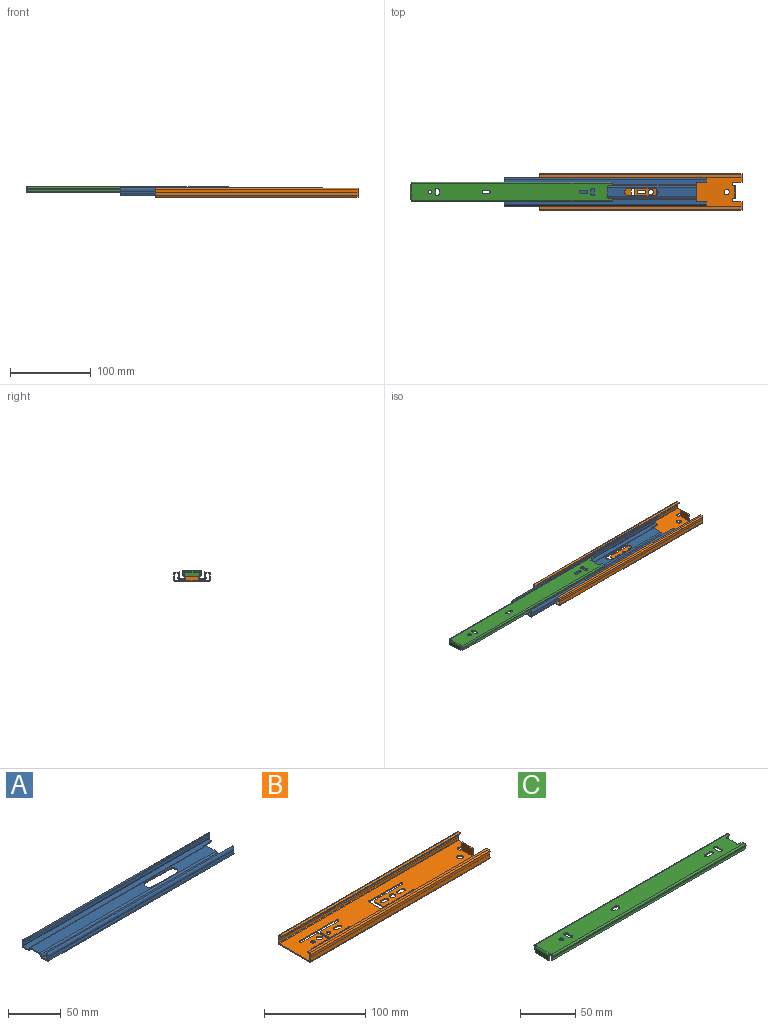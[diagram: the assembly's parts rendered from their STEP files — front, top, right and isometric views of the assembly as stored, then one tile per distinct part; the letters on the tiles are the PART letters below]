
ASSEMBLY  parts=3 mates=2
PART A: 42 faces, bbox 249.9x35.2x9.3 mm
  f0: cylinder r=4.83mm len=9.65mm, axis (0,0,1), area 18.5mm2, adj f1,f16,f23,f41
  f1: plane 237.24x12.23mm, normal (0,0,-1), area 2522.2mm2, adj f0,f2,f18,f20,f22,f23,f24,f41
  f2: cylinder r=0.76mm len=237.24mm, axis (-1,0,0), area 205.1mm2, adj f1,f3,f18,f20
  f3: plane 237.24x1.97mm, normal (0,-0.91,-0.42), area 516.2mm2, adj f2,f4,f18,f20
  f4: cylinder r=1.98mm len=237.24mm, axis (-1,0,0), area 533.2mm2, adj f3,f5,f18,f20
  f5: plane 249.94x6.86mm, normal (0,0,-1), area 1682.4mm2, adj f4,f6,f17,f18,f19,f20,f21
  f6: cylinder r=1.22mm len=249.94mm, axis (-1,0,0), area 698.7mm2, adj f5,f7,f17,f18
  f7: cylinder r=2.51mm len=249.94mm, axis (-1,0,0), area 734.3mm2, adj f6,f8,f17,f18
  f8: cylinder r=3.52mm len=249.94mm, axis (-1,0,0), area 1279.5mm2, adj f7,f9,f17,f18
  f9: plane 249.94x1.03mm, normal (0,-0.84,0.54), area 304.7mm2, adj f8,f10,f17,f18
  f10: cylinder r=2.3mm len=249.94mm, axis (-1,0,0), area 836mm2, adj f9,f11,f17,f18
  f11: cylinder r=3.73mm len=249.94mm, axis (-1,0,0), area 1091.1mm2, adj f10,f12,f17,f18
  f12: plane 249.94x6.86mm, normal (0,0,1), area 1682.4mm2, adj f11,f13,f17,f18,f19,f20,f21
  f13: cylinder r=0.76mm len=237.24mm, axis (-1,0,0), area 205.1mm2, adj f12,f14,f18,f20
  f14: plane 237.24x1.97mm, normal (0,0.91,0.42), area 516.2mm2, adj f13,f15,f18,f20
  f15: cylinder r=1.98mm len=237.24mm, axis (-1,0,0), area 533.2mm2, adj f14,f16,f18,f20
  f16: plane 237.24x12.23mm, normal (0,0,1), area 2522.2mm2, adj f0,f15,f18,f20,f22,f23,f37,f41
  f17: plane 9.27x5.53mm, normal (1,0,0), area 16.6mm2, adj f5,f6,f7,f8,f9,f10,f11,f12
  f18: plane 35.19x9.27mm, normal (-1,0,0), area 67.2mm2, adj f1,f2,f3,f4,f5,f6,f7,f8
  f19: cylinder r=2.54mm len=2.54mm, axis (0,0,1), area 4.9mm2, adj f5,f12,f20,f21
  f20: plane 19.05x4.78mm, normal (1,0,0), area 27.8mm2, adj f1,f2,f3,f4,f5,f12,f13,f14
  f21: plane 10.16x1.22mm, normal (0,-1,0), area 12.4mm2, adj f5,f12,f17,f19
  f22: cylinder r=4.83mm len=9.65mm, axis (0,0,1), area 18.5mm2, adj f1,f16,f23,f41
  f23: plane 31.75x1.22mm, normal (0,-1,0), area 38.7mm2, adj f0,f1,f16,f22
  f24: cylinder r=0.76mm len=237.24mm, axis (-1,0,0), area 205.1mm2, adj f1,f18,f20,f25
  f25: plane 237.24x1.97mm, normal (0,0.91,-0.42), area 516.2mm2, adj f18,f20,f24,f26
  f26: cylinder r=1.98mm len=237.24mm, axis (-1,0,0), area 533.2mm2, adj f18,f20,f25,f27
  f27: plane 249.94x6.86mm, normal (0,0,-1), area 1682.4mm2, adj f18,f20,f26,f28,f38,f39,f40
  f28: cylinder r=1.22mm len=249.94mm, axis (-1,0,0), area 698.7mm2, adj f18,f27,f29,f38
  f29: cylinder r=2.51mm len=249.94mm, axis (-1,0,0), area 734.3mm2, adj f18,f28,f30,f38
  f30: cylinder r=3.52mm len=249.94mm, axis (-1,0,0), area 1279.5mm2, adj f18,f29,f31,f38
  f31: plane 249.94x1.03mm, normal (0,0.84,0.54), area 304.7mm2, adj f18,f30,f32,f38
  f32: cylinder r=2.3mm len=249.94mm, axis (-1,0,0), area 836mm2, adj f18,f31,f33,f38
  f33: cylinder r=3.73mm len=249.94mm, axis (-1,0,0), area 1091.1mm2, adj f18,f32,f34,f38
  f34: plane 249.94x6.86mm, normal (0,0,1), area 1682.4mm2, adj f18,f20,f33,f35,f38,f39,f40
  f35: cylinder r=0.76mm len=237.24mm, axis (-1,0,0), area 205.1mm2, adj f18,f20,f34,f36
  f36: plane 237.24x1.97mm, normal (0,-0.91,0.42), area 516.2mm2, adj f18,f20,f35,f37
  f37: cylinder r=1.98mm len=237.24mm, axis (-1,0,0), area 533.2mm2, adj f16,f18,f20,f36
  f38: plane 9.27x5.53mm, normal (1,0,0), area 16.6mm2, adj f27,f28,f29,f30,f31,f32,f33,f34
  f39: cylinder r=2.54mm len=2.54mm, axis (0,0,1), area 4.9mm2, adj f20,f27,f34,f40
  f40: plane 10.16x1.22mm, normal (0,1,0), area 12.4mm2, adj f27,f34,f38,f39
  f41: plane 31.75x1.22mm, normal (0,1,0), area 38.7mm2, adj f0,f1,f16,f22
PART B: 85 faces, bbox 249.9x45.6x11.3 mm
  f0: cylinder r=1.59mm len=3.18mm, axis (0,0,1), area 6mm2, adj f8,f9,f72,f73
  f1: cylinder r=3.17mm len=6.35mm, axis (0,0,-1), area 23.8mm2, adj f8,f9
  f2: cylinder r=3.17mm len=6.35mm, axis (0,0,-1), area 23.8mm2, adj f8,f9
  f3: cylinder r=2.29mm len=4.57mm, axis (0,0,1), area 8.6mm2, adj f8,f9,f40,f77
  f4: cylinder r=2.29mm len=4.57mm, axis (0,0,1), area 17.1mm2, adj f8,f9
  f5: cylinder r=3.17mm len=6.35mm, axis (0,0,1), area 23.8mm2, adj f8,f9
  f6: cylinder r=2.29mm len=4.57mm, axis (0,0,1), area 17.1mm2, adj f8,f9
  f7: cylinder r=1.59mm len=3.18mm, axis (0,0,1), area 6mm2, adj f8,f9,f32,f33
  f8: plane 249.94x42.24mm, normal (0,0,1), area 9331.9mm2, adj f0,f1,f2,f3,f4,f5,f6,f7
  f9: plane 249.94x42.24mm, normal (0,0,-1), area 9352.8mm2, adj f0,f1,f2,f3,f4,f5,f6,f7
  f10: cylinder r=1.7mm len=249.94mm, axis (-1,0,0), area 679.3mm2, adj f9,f11,f22,f23
  f11: plane 249.94x4.64mm, normal (0,1,0.03), area 1159mm2, adj f10,f12,f22,f23
  f12: plane 249.94x3.4mm, normal (0,1,-0.04), area 849.3mm2, adj f11,f13,f22,f23
  f13: cylinder r=1.45mm len=249.94mm, axis (-1,0,0), area 581.3mm2, adj f12,f14,f22,f23
  f14: plane 249.94x2.96mm, normal (0,0,1), area 739.4mm2, adj f13,f15,f22,f23
  f15: plane 249.94x1.19mm, normal (0,-1,0), area 298.4mm2, adj f14,f16,f22,f23
  f16: plane 249.94x2.96mm, normal (0,0,-1), area 739.4mm2, adj f15,f17,f22,f23
  f17: cylinder r=0.25mm len=249.94mm, axis (-1,0,0), area 102mm2, adj f16,f18,f22,f23
  f18: plane 249.94x3.05mm, normal (0,-1,0.04), area 763mm2, adj f17,f19,f22,f23
  f19: cylinder r=2.54mm len=249.94mm, axis (-1,0,0), area 484.9mm2, adj f18,f20,f22,f23
  f20: plane 249.94x3.16mm, normal (0,-1,-0.03), area 790.5mm2, adj f19,f21,f22,f23
  f21: cylinder r=0.51mm len=249.94mm, axis (-1,0,0), area 202.8mm2, adj f8,f20,f22,f23
  f22: plane 11.28x10.62mm, normal (1,0,0), area 27.3mm2, adj f8,f9,f10,f11,f12,f13,f14,f15
  f23: plane 45.64x11.28mm, normal (-1,0,0), area 83.7mm2, adj f8,f9,f10,f11,f12,f13,f14,f15
  f24: plane 14.99x10.08mm, normal (1,0,0), area 151.1mm2, adj f9,f25,f28,f30,f67,f70
  f25: plane 1.43x1.19mm, normal (0.11,0.99,0), area 1.7mm2, adj f8,f9,f24,f26
  f26: cylinder r=2.29mm len=4.56mm, axis (0,0,1), area 8.3mm2, adj f8,f9,f25,f27
  f27: plane 9.4x1.19mm, normal (0,-1,0), area 11.2mm2, adj f8,f9,f22,f26
  f28: plane 8.89x1.4mm, normal (0,1,0), area 12.4mm2, adj f8,f24,f29,f30
  f29: plane 14.99x8.89mm, normal (-1,0,0), area 133.2mm2, adj f8,f28,f30,f70
  f30: plane 14.99x1.4mm, normal (0,0,1), area 20.9mm2, adj f24,f28,f29,f70
  f31: cylinder r=1.59mm len=3.18mm, axis (0,0,1), area 6mm2, adj f8,f9,f32,f38
  f32: plane 50.93x1.19mm, normal (0,-1,0), area 60.8mm2, adj f7,f8,f9,f31
  f33: plane 24.83x1.19mm, normal (0,1,0), area 29.6mm2, adj f7,f8,f9,f34
  f34: cylinder r=0.76mm len=1.19mm, axis (0,0,1), area 1.4mm2, adj f8,f9,f33,f35
  f35: plane 12.7x1.19mm, normal (-1,0,0), area 15.2mm2, adj f8,f9,f34,f74
  f36: plane 12.7x1.19mm, normal (1,0,0), area 15.2mm2, adj f8,f9,f37,f75
  f37: cylinder r=0.76mm len=1.19mm, axis (0,0,1), area 1.4mm2, adj f8,f9,f36,f38
  f38: plane 22.29x1.19mm, normal (0,1,0), area 26.6mm2, adj f8,f9,f31,f37
  f39: cylinder r=2.29mm len=4.57mm, axis (0,0,1), area 8.6mm2, adj f8,f9,f40,f77
  f40: plane 5.08x1.19mm, normal (0,-1,0), area 6.1mm2, adj f3,f8,f9,f39
  f41: cylinder r=1.59mm len=3.18mm, axis (0,0,-1), area 6mm2, adj f8,f9,f42,f47
  f42: plane 43.24x1.19mm, normal (0,-1,0), area 51.6mm2, adj f8,f9,f41,f43
  f43: cylinder r=1.52mm len=1.52mm, axis (0,0,-1), area 2.9mm2, adj f8,f9,f42,f44
  f44: plane 17.53x1.19mm, normal (1,0,0), area 20.9mm2, adj f8,f9,f43,f80
  f45: plane 11.18x1.19mm, normal (-1,0,0), area 13.3mm2, adj f8,f9,f46,f81
  f46: cylinder r=1.52mm len=1.52mm, axis (0,0,-1), area 2.9mm2, adj f8,f9,f45,f47
  f47: plane 38.67x1.19mm, normal (0,1,0), area 46.2mm2, adj f8,f9,f41,f46
  f48: cylinder r=2.29mm len=4.57mm, axis (0,0,-1), area 8.6mm2, adj f8,f9,f49,f83
  f49: plane 5.08x1.19mm, normal (0,-1,0), area 6.1mm2, adj f8,f9,f48,f50
  f50: cylinder r=2.29mm len=4.57mm, axis (0,0,-1), area 8.6mm2, adj f8,f9,f49,f83
  f51: cylinder r=2.29mm len=4.57mm, axis (0,0,-1), area 8.6mm2, adj f8,f9,f52,f84
  f52: plane 5.08x1.19mm, normal (0,-1,0), area 6.1mm2, adj f8,f9,f51,f53
  f53: cylinder r=2.29mm len=4.57mm, axis (0,0,-1), area 8.6mm2, adj f8,f9,f52,f84
  f54: cylinder r=1.7mm len=249.94mm, axis (-1,0,0), area 679.3mm2, adj f9,f23,f55,f66
  f55: plane 249.94x4.64mm, normal (0,-1,0.03), area 1159mm2, adj f23,f54,f56,f66
  f56: plane 249.94x3.4mm, normal (0,-1,-0.04), area 849.3mm2, adj f23,f55,f57,f66
  f57: cylinder r=1.45mm len=249.94mm, axis (-1,0,0), area 581.3mm2, adj f23,f56,f58,f66
  f58: plane 249.94x2.96mm, normal (0,0,1), area 739.4mm2, adj f23,f57,f59,f66
  f59: plane 249.94x1.19mm, normal (0,1,0), area 298.4mm2, adj f23,f58,f60,f66
  f60: plane 249.94x2.96mm, normal (0,0,-1), area 739.4mm2, adj f23,f59,f61,f66
  f61: cylinder r=0.25mm len=249.94mm, axis (-1,0,0), area 102mm2, adj f23,f60,f62,f66
  f62: plane 249.94x3.05mm, normal (0,1,0.04), area 763mm2, adj f23,f61,f63,f66
  f63: cylinder r=2.54mm len=249.94mm, axis (-1,0,0), area 484.9mm2, adj f23,f62,f64,f66
  f64: plane 249.94x3.16mm, normal (0,1,-0.03), area 790.5mm2, adj f23,f63,f65,f66
  f65: cylinder r=0.51mm len=249.94mm, axis (-1,0,0), area 202.8mm2, adj f8,f23,f64,f66
  f66: plane 11.28x10.62mm, normal (1,0,0), area 27.3mm2, adj f8,f9,f54,f55,f56,f57,f58,f59
  f67: plane 1.43x1.19mm, normal (0.11,-0.99,0), area 1.7mm2, adj f8,f9,f24,f68
  f68: cylinder r=2.29mm len=4.56mm, axis (0,0,1), area 8.3mm2, adj f8,f9,f67,f69
  f69: plane 9.4x1.19mm, normal (0,1,0), area 11.2mm2, adj f8,f9,f66,f68
  f70: plane 8.89x1.4mm, normal (0,-1,0), area 12.4mm2, adj f8,f24,f29,f30
  f71: cylinder r=1.59mm len=3.18mm, axis (0,0,1), area 6mm2, adj f8,f9,f72,f76
  f72: plane 50.93x1.19mm, normal (0,1,0), area 60.8mm2, adj f0,f8,f9,f71
  f73: plane 24.83x1.19mm, normal (0,-1,0), area 29.6mm2, adj f0,f8,f9,f74
  f74: cylinder r=0.76mm len=1.19mm, axis (0,0,1), area 1.4mm2, adj f8,f9,f35,f73
  f75: cylinder r=0.76mm len=1.19mm, axis (0,0,1), area 1.4mm2, adj f8,f9,f36,f76
  f76: plane 22.29x1.19mm, normal (0,-1,0), area 26.6mm2, adj f8,f9,f71,f75
  f77: plane 5.08x1.19mm, normal (0,1,0), area 6.1mm2, adj f3,f8,f9,f39
  f78: cylinder r=1.59mm len=3.18mm, axis (0,0,-1), area 6mm2, adj f8,f9,f79,f82
  f79: plane 43.24x1.19mm, normal (0,1,0), area 51.6mm2, adj f8,f9,f78,f80
  f80: cylinder r=1.52mm len=1.52mm, axis (0,0,-1), area 2.9mm2, adj f8,f9,f44,f79
  f81: cylinder r=1.52mm len=1.52mm, axis (0,0,-1), area 2.9mm2, adj f8,f9,f45,f82
  f82: plane 38.67x1.19mm, normal (0,-1,0), area 46.2mm2, adj f8,f9,f78,f81
  f83: plane 5.08x1.19mm, normal (0,1,0), area 6.1mm2, adj f8,f9,f48,f50
  f84: plane 5.08x1.19mm, normal (0,1,0), area 6.1mm2, adj f8,f9,f51,f53
PART C: 54 faces, bbox 249.9x24.3x6.8 mm
  f0: cylinder r=2.16mm len=4.32mm, axis (0,0,1), area 9.5mm2, adj f3,f13,f34,f53
  f1: cylinder r=2.16mm len=4.32mm, axis (0,0,1), area 9.5mm2, adj f3,f13,f29,f51
  f2: cylinder r=2.29mm len=4.57mm, axis (0,0,1), area 20.1mm2, adj f3,f13
  f3: plane 248.29x21.25mm, normal (0,0,-1), area 5015.5mm2, adj f0,f1,f2,f4,f14,f15,f16,f21
  f4: cylinder r=0.13mm len=248.03mm, axis (-1,0,0), area 49.5mm2, adj f3,f5,f14,f15
  f5: plane 248.03x0.37mm, normal (0,-1,0), area 92.5mm2, adj f4,f6,f14,f15
  f6: cylinder r=0.13mm len=248.03mm, axis (-1,0,0), area 20.6mm2, adj f5,f7,f14,f15
  f7: cylinder r=3.81mm len=248.03mm, axis (-1,0,0), area 1283.1mm2, adj f6,f8,f14,f15
  f8: plane 248.03x1.07mm, normal (0,0.65,-0.76), area 346.5mm2, adj f7,f9,f14,f15
  f9: cylinder r=2.41mm len=248.03mm, axis (-1,0,0), area 812.4mm2, adj f8,f10,f14,f15
  f10: cylinder r=1.52mm len=248.03mm, axis (-1,0,0), area 247.4mm2, adj f9,f11,f14,f15
  f11: plane 248.03x0.37mm, normal (0,1,0), area 92.5mm2, adj f10,f12,f14,f15
  f12: cylinder r=1.52mm len=248.03mm, axis (-1,0,0), area 593.8mm2, adj f11,f13,f14,f15
  f13: plane 248.29x21.25mm, normal (0,0,1), area 5015.5mm2, adj f0,f1,f2,f12,f14,f15,f20,f21
  f14: plane 6.76x3.56mm, normal (1,0,0), area 11.8mm2, adj f3,f4,f5,f6,f7,f8,f9,f10
  f15: plane 6.76x3.26mm, normal (-1,0,0), area 11.4mm2, adj f3,f4,f5,f6,f7,f8,f9,f10
  f16: cylinder r=0.25mm len=17.78mm, axis (0,-1,0), area 7.1mm2, adj f3,f17,f21,f46
  f17: plane 17.78x5.11mm, normal (1,0,0), area 90.8mm2, adj f16,f18,f21,f46
  f18: plane 17.78x1.4mm, normal (0,0,-1), area 24.8mm2, adj f17,f19,f21,f46
  f19: plane 17.78x5.11mm, normal (-1,0,0), area 90.8mm2, adj f18,f20,f21,f46
  f20: cylinder r=1.65mm len=17.78mm, axis (0,-1,0), area 46.1mm2, adj f13,f19,f21,f46
  f21: plane 6.76x1.91mm, normal (0,1,0), area 9.6mm2, adj f3,f13,f15,f16,f17,f18,f19,f20
  f22: cylinder r=0.63mm len=1.4mm, axis (0,0,1), area 2.6mm2, adj f3,f13,f23,f24
  f23: plane 5.86x1.4mm, normal (0.23,-0.97,0), area 8.4mm2, adj f3,f13,f14,f22
  f24: plane 5.97x1.4mm, normal (1,0,0), area 8.3mm2, adj f3,f13,f22,f49
  f25: cylinder r=2.16mm len=4.32mm, axis (0,0,1), area 9.5mm2, adj f3,f13,f26,f27
  f26: plane 5.33x1.4mm, normal (-1,0,0), area 7.5mm2, adj f3,f13,f25,f50
  f27: plane 5.33x1.4mm, normal (1,0,0), area 7.5mm2, adj f3,f13,f25,f50
  f28: cylinder r=2.16mm len=4.32mm, axis (0,0,1), area 9.5mm2, adj f3,f13,f29,f51
  f29: plane 5.33x1.4mm, normal (0,-1,0), area 7.5mm2, adj f1,f3,f13,f28
  f30: plane 5.33x1.4mm, normal (1,0,0), area 7.5mm2, adj f3,f13,f31,f52
  f31: cylinder r=2.16mm len=4.32mm, axis (0,0,1), area 9.5mm2, adj f3,f13,f30,f32
  f32: plane 5.33x1.4mm, normal (-1,0,0), area 7.5mm2, adj f3,f13,f31,f52
  f33: cylinder r=2.16mm len=4.32mm, axis (0,0,1), area 9.5mm2, adj f3,f13,f34,f53
  f34: plane 5.33x1.4mm, normal (0,-1,0), area 7.5mm2, adj f0,f3,f13,f33
  f35: cylinder r=0.13mm len=248.03mm, axis (-1,0,0), area 49.5mm2, adj f3,f36,f44,f45
  f36: plane 248.03x0.37mm, normal (0,1,0), area 92.5mm2, adj f35,f37,f44,f45
  f37: cylinder r=0.13mm len=248.03mm, axis (-1,0,0), area 20.6mm2, adj f36,f38,f44,f45
  f38: cylinder r=3.81mm len=248.03mm, axis (-1,0,0), area 1283.1mm2, adj f37,f39,f44,f45
  f39: plane 248.03x1.07mm, normal (0,-0.65,-0.76), area 346.5mm2, adj f38,f40,f44,f45
  f40: cylinder r=2.41mm len=248.03mm, axis (-1,0,0), area 812.4mm2, adj f39,f41,f44,f45
  f41: cylinder r=1.52mm len=248.03mm, axis (-1,0,0), area 247.4mm2, adj f40,f42,f44,f45
  f42: plane 248.03x0.37mm, normal (0,-1,0), area 92.5mm2, adj f41,f43,f44,f45
  f43: cylinder r=1.52mm len=248.03mm, axis (-1,0,0), area 593.8mm2, adj f13,f42,f44,f45
  f44: plane 6.76x3.56mm, normal (1,0,0), area 11.8mm2, adj f3,f13,f35,f36,f37,f38,f39,f40
  f45: plane 6.76x3.26mm, normal (-1,0,0), area 11.4mm2, adj f3,f13,f35,f36,f37,f38,f39,f40
  f46: plane 6.76x1.91mm, normal (0,-1,0), area 9.6mm2, adj f3,f13,f16,f17,f18,f19,f20,f45
  f47: cylinder r=0.63mm len=1.4mm, axis (0,0,1), area 2.6mm2, adj f3,f13,f48,f49
  f48: plane 5.86x1.4mm, normal (0.23,0.97,0), area 8.4mm2, adj f3,f13,f44,f47
  f49: plane 5.97x1.4mm, normal (1,0,0), area 8.3mm2, adj f3,f13,f24,f47
  f50: cylinder r=2.16mm len=4.32mm, axis (0,0,1), area 9.5mm2, adj f3,f13,f26,f27
  f51: plane 5.33x1.4mm, normal (0,1,0), area 7.5mm2, adj f1,f3,f13,f28
  f52: cylinder r=2.16mm len=4.32mm, axis (0,0,1), area 9.5mm2, adj f3,f13,f30,f32
  f53: plane 5.33x1.4mm, normal (0,1,0), area 7.5mm2, adj f0,f3,f13,f33
PLACE A t=(-275.76,-351.41,-110.38)mm
PLACE B t=(-356.8,-351.41,-110.57)mm fixed
PLACE C t=(-267.38,-351.41,-110.47)mm
MATE slider A.f18 <-> B.f23  axis (-1,0,0) through (-525.74,-351.41,-109.13)mm
MATE slider C.f19 <-> A.f18  axis (-1,0,0) through (-642.38,-351.41,-107.61)mm
